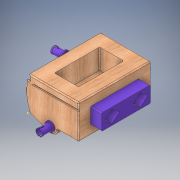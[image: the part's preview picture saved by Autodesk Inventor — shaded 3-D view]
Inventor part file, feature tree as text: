
AUTODESK INVENTOR PART (.ipt)
format: ipt  version: 2018 (Build 220112000, 112)  size: 1,092,608 bytes
history: native  units: in
note: dims shown in document units (in); Inventor stores cm internally (conversion verified against a paired STEP export)
features: sketch x38, extrude x36, projected_geometry x15, fillet x5
ambient origin geometry x8: Origin, YZ Plane, XZ Plane, XY Plane, X Axis, Y Axis, Z Axis, Center Point
bodies: Solid1 (feature_tree)
feature tree (94):
  extrude  "Extrusion1"  Depth=2.205in
  extrude  "Extrusion2"  Depth=0.05in
  sketch  "Sketch3"  dims[d4=0.94in d5=1.156in]
  sketch  "Sketch4"  dims[d6=0.307in d9=0.05in]
  extrude  "Extrusion3"  Depth=1.156in
  extrude  "Extrusion4"  Depth=0.05in
  extrude  "Extrusion5"  Depth=0.15in
  extrude  "Extrusion6"  Depth=0.009in
  extrude  "Extrusion7"  Depth=3.23in TaperAngle=0.0deg
  fillet  "Fillet1"  Radius=0.065in
  fillet  "Fillet2"  Radius=0.065in
  extrude  "Extrusion8"  Depth=0.125in
  extrude  "Extrusion9"  Depth=3.71in TaperAngle=0.0deg
  extrude  "Extrusion10"  Depth=0.275in
  extrude  "Extrusion11"  Depth=0.275in
  extrude  "Extrusion12"  Depth=0.155in
  extrude  "Extrusion13"  Depth=0.1263in
  extrude  "Extrusion14"  Depth=0.1263in
  extrude  "Extrusion15"  Depth=0.025in TaperAngle=0.0deg
  sketch  "Sketch17"  dims[d52=5.0in d53=0.0in d54=0.5in d55=0.125in]
  extrude  "Extrusion16"  Depth=0.4in
  fillet  "Fillet3"  Radius=0.025in
  extrude  "Extrusion17"  Depth=0.5in
  fillet  "Fillet4"  Radius=0.125in
  extrude  "Extrusion18"  Depth=0.25in TaperAngle=0.0deg
  fillet  "Fillet5"  Radius=2.19in
  extrude  "Extrusion19"  Depth=0.01in
  extrude  "Extrusion20"  Depth=0.25in TaperAngle=0.0deg
  extrude  "Extrusion21"  Depth=0.06in TaperAngle=0.0deg
  extrude  "Extrusion22"  Depth=0.385in TaperAngle=0.0deg
  extrude  "Extrusion23"  Depth=0.385in
  extrude  "Extrusion24"  Depth=0.06in
  extrude  "Extrusion25"  Depth=0.445in
  extrude  "Extrusion26"  Depth=0.214in TaperAngle=0.0deg
  extrude  "Extrusion27"  Depth=0.05in
  extrude  "Extrusion28"  Depth=0.3in
  extrude  "Extrusion29"  Depth=0.28in
  extrude  "Extrusion30"  Depth=0.14in
  extrude  "Extrusion31"  Depth=0.14in
  extrude  "Extrusion32"  Depth=0.28in
  extrude  "Extrusion33"  Depth=0.14in
  extrude  "Extrusion34"  Depth=0.615in
  extrude  "Extrusion35"  Depth=3.23in
  extrude  "Extrusion36"  Depth=0.515in
  sketch  "Sketch1"  dims[d0=1.517in d1=2.205in]
  sketch  "Sketch2"  dims[d2=0.255in d3=0.05in]
  sketch  "Sketch5"  dims[d10=1.175in d11=0.15in]
  projected_geometry  "Projected Loop1"
  sketch  "Sketch6"  dims[d12=0.05in d13=0.009in]
  sketch  "Sketch7"  dims[d14=0.025in d15=3.23in d16=0.0in d18=0.065in d19=0.065in]
  projected_geometry  "Projected Loop2"
  projected_geometry  "Projected Loop3"
  projected_geometry  "Projected Loop4"
  projected_geometry  "Projected Loop5"
  projected_geometry  "Projected Loop6"
  sketch  "Sketch8"  dims[d26=0.54in d27=0.125in]
  sketch  "Sketch9"  dims[d28=2.71in d29=0.0in d30=3.71in d31=0.0in]
  sketch  "Sketch10"  dims[d32=1.52in d33=0.0in d36=0.275in]
  sketch  "Sketch11"  dims[d37=0.1263in d38=0.275in]
  projected_geometry  "Projected Loop7"
  sketch  "Sketch12"  dims[d39=0.1263in d40=0.155in]
  sketch  "Sketch13"  dims[d41=0.275in d42=0.1263in]
  sketch  "Sketch14"  dims[d43=0.275in d44=0.1263in]
  sketch  "Sketch15"  dims[d45=0.275in d46=0.025in d47=0.0in]
  sketch  "Sketch16"  dims[d48=0.4in d49=0.0in d50=0.025in d51=0.025in]
  sketch  "Sketch18"  dims[d56=0.5in d57=0.0in d58=0.25in d59=0.0in d60=2.19in]
  sketch  "Sketch19"  dims[d61=1.095in d62=0.01in]
  sketch  "Sketch20"  dims[d63=0.86in d64=0.25in d65=0.0in]
  sketch  "Sketch21"  dims[d66=0.41in d67=0.06in d68=0.0in]
  projected_geometry  "Projected Loop8"
  sketch  "Sketch22"  dims[d69=0.295in d70=0.385in d71=0.0in]
  sketch  "Sketch23"  dims[d72=0.385in d73=0.0in d74=0.31in]
  sketch  "Sketch24"  dims[d75=0.06in d76=0.0in d77=0.285in]
  sketch  "Sketch25"  dims[d78=0.445in d79=0.0in d80=0.022in]
  sketch  "Sketch26"  dims[d81=0.022in d82=0.214in d83=0.0in]
  projected_geometry  "Projected Loop9"
  sketch  "Sketch27"  dims[d84=0.05in d85=0.14in]
  sketch  "Sketch28"  dims[d86=0.14in d87=0.3in]
  projected_geometry  "Projected Loop10"
  sketch  "Sketch29"  dims[d88=0.3in d91=0.28in]
  sketch  "Sketch30"  dims[d92=0.25in d93=0.0in d94=0.14in]
  projected_geometry  "Projected Loop11"
  sketch  "Sketch31"  dims[d95=0.235in d96=0.14in]
  sketch  "Sketch32"  dims[d97=0.28in d98=0.28in]
  sketch  "Sketch33"  dims[d99=0.41in d100=0.0in d101=0.14in]
  sketch  "Sketch34"  dims[d102=4.0in d103=0.0in d104=0.615in]
  sketch  "Sketch35"  dims[d105=0.6091in d106=3.23in]
  projected_geometry  "Projected Loop12"
  sketch  "Sketch36"  dims[d107=0.615in d108=0.515in]
  projected_geometry  "Projected Loop13"
  projected_geometry  "Projected Loop14"
  projected_geometry  "Projected Loop15"
  sketch  "Sketch37"  dims[d109=0.05in]
  sketch  "Sketch38"  dims[d110=0.905in d111=0.0in d112=1.247in d113=0.41in d114=0.06in d115=0.0in d116=0.06in d117=0.0in d118=0.295in d119=0.385in d120=0.0in d121=0.385in d122=0.0in d123=0.31in d124=0.06in d125=0.0in d126=0.06in d127=0.0in d128=0.285in d129=0.445in d130=0.0in d131=0.445in d132=0.0in d133=0.022in d134=0.044in d135=0.214in d136=0.0in d137=0.214in d138=0.0in d139=0.52in d140=0.52in d141=0.395in d142=0.395in d143=0.05in d144=0.14in d145=0.14in d146=0.364in d147=0.364in d148=0.65in d149=0.65in d150=0.095in d151=0.095in d152=0.095in d153=0.095in d154=0.325in d155=0.325in d156=0.465in d157=0.465in d158=0.465in d159=0.465in d160=0.465in d161=0.495in d162=0.0in d163=0.267in d164=0.07in d165=2.095in d166=0.05in d167=0.0in d168=0.05in d169=0.0in d170=0.005in d171=0.005in d172=0.005in d173=0.005in d174=0.005in d175=0.005in d176=0.005in d177=0.005in d178=0.005in d179=0.005in d180=0.005in d181=0.005in d182=0.005in d183=0.005in d184=0.005in d185=0.005in d186=180.0deg d188=180.0deg d189=0.005in d190=0.005in d191=0.005in d192=0.005in d193=180.0deg d194=180.0deg d195=180.0deg d196=0.0in d197=180.0deg d198=0.05in d199=0.495in d200=0.0in d201=0.52in d202=0.52in d203=0.395in d204=0.395in d205=0.005in d206=0.005in d207=0.005in d208=0.005in d209=0.005in d210=0.005in d211=0.005in d212=0.005in d213=0.005in d214=0.005in d215=0.005in d216=0.005in d217=0.005in d218=0.005in d219=0.005in d220=0.005in d221=0.005in d222=0.005in d223=0.005in d224=0.005in d225=0.005in d226=0.005in d227=0.005in d228=0.005in d229=180.0deg d230=180.0deg d231=180.0deg d232=180.0deg d233=0.0in d234=180.0deg d235=0.0in d236=0.05in d237=0.05in d238=0.05in d239=0.495in d240=0.0in d241=0.52in d242=0.52in d243=0.395in d244=0.395in d245=0.005in d246=0.005in d247=0.005in d248=0.005in d249=0.005in d250=0.005in d251=0.005in d252=0.005in d253=0.005in d254=0.005in d255=0.005in d256=0.005in d257=0.005in d258=0.005in d259=0.005in d260=0.005in d261=0.005in d262=0.005in d263=0.005in d264=0.005in d265=0.005in d266=0.005in d267=0.005in d268=0.005in d269=180.0deg d270=180.0deg d271=180.0deg d272=180.0deg d273=0.0in d274=180.0deg d275=0.0in d276=0.05in d277=0.05in d278=0.05in d279=0.495in d280=0.0in]
